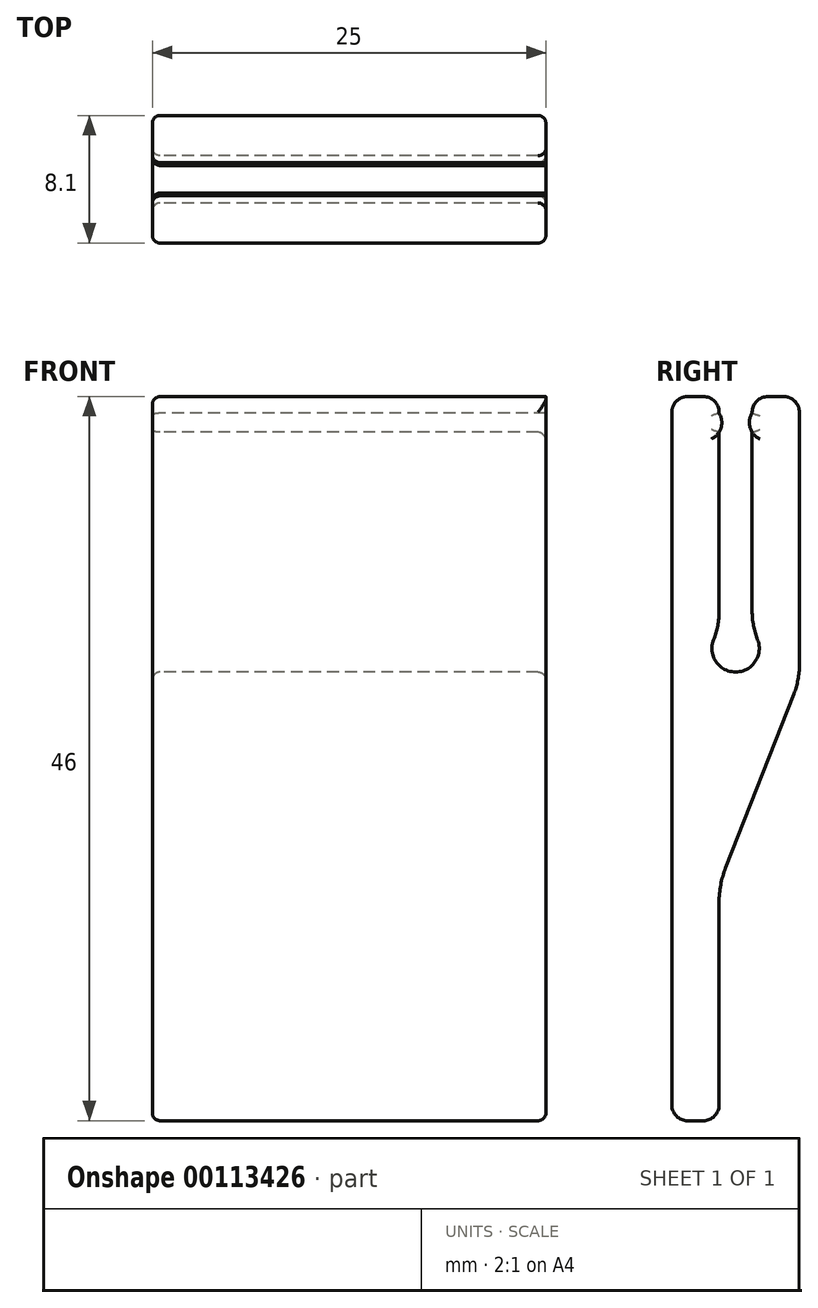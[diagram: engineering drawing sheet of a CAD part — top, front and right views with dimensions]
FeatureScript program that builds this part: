
annotation { "Feature Type Name" : "Feature", "Feature Type Description" : "" }
export const myFeature = defineFeature(function(context is Context, id is Id, definition is map)
    precondition{}
    {
        {
            var Q0;
            Q0=qCreatedBy(makeId("Right.planeOp"),FACE);
            var sketch = newSketch(context, id + "F0", { "sketchPlane" : qUnion([Q0])});
            skLineSegment(sketch, "E0.bottom", {"start": v(-2.62, 41.62) * mm, "end": v(0.38, 41.62) * mm});
            skLineSegment(sketch, "E0.left", {"start": v(-2.62, 41.62) * mm, "end": v(-2.62, 25.62) * mm});
            skLineSegment(sketch, "E0.right", {"start": v(5.48, 41.62) * mm, "end": v(5.48, 23.62) * mm});
            skLineSegment(sketch, "E1.top", {"start": v(-2.62, -4.38) * mm, "end": v(0.38, -4.38) * mm});
            skLineSegment(sketch, "E1.left", {"start": v(-2.62, 25.62) * mm, "end": v(-2.62, -4.38) * mm});
            skLineSegment(sketch, "E1.right", {"start": v(0.38, 9.48) * mm, "end": v(0.38, -4.38) * mm});
            skLineSegment(sketch, "E2.left", {"start": v(0.38, 41.62) * mm, "end": v(0.38, 26.69) * mm});
            skLineSegment(sketch, "E2.right", {"start": v(2.48, 41.62) * mm, "end": v(2.48, 26.69) * mm});
            skLineSegment(sketch, "E3.trimOffspring", {"start": v(2.48, 41.62) * mm, "end": v(5.48, 41.62) * mm});
            skLineSegment(sketch, "E4", {"start": v(5.48, 23.62) * mm, "end": v(0.8, 11.67) * mm});
            skLineSegment(sketch, "E5.filletArc", {"start": v(0.6, 24.36) * mm, "end": v(0.6, 24.36) * mm});
            skPoint(sketch, "E6.visualSharp", {"position": v(0.38, 10.62) * mm});
            skArc(sketch, "E6.filletArc", {"start": v(0.8, 11.67) * mm, "mid": v(0.48, 10.6) * mm, "end": v(0.38, 9.48) * mm});
            skArc(sketch, "E7", {"start": v(0.38, 26.69) * mm, "mid": v(1.43, 24.12) * mm, "end": v(2.48, 26.69) * mm});
            skLineSegment(sketch, "E8", {"start": v(0.38, 25.62) * mm, "end": v(2.48, 25.62) * mm, "construction": true});
            skCircle(sketch, "E9", {"center": v(-0.57, 39.95) * mm, "radius": 1.13 * mm});
            skLineSegment(sketch, "E10", {"start": v(1.43, 25.62) * mm, "end": v(1.43, 44.61) * mm, "construction": true});
            skCircle(sketch, "E11.MirrorC", {"center": v(3.43, 39.95) * mm, "radius": 1.13 * mm});
            skLineSegment(sketch, "E12", {"start": v(0.38, 28.92) * mm, "end": v(2.48, 28.92) * mm, "construction": true});
            skPoint(sketch, "E13", {"position": v(1.43, 28.92) * mm});
            skSolve(sketch);
        }
        {
            var Q0;
            Q0 = qSketchRegion(id + "F0", true);
            extrude(context, id + "F1", {"entities" : qUnion([Q0]), "depth" : 25 * mm});
        }
        {
            var Q0;
            Q0=makeQuery(id+"F1.opExtrude","SWEPT_EDGE",EDGE,{"disambiguationData":[OSD([sQuery(id+"F0.wireOp",EDGE,"E2.left"),sQuery(id+"F0.wireOp",EDGE,"E7")])]});
            var Q1;
            Q1=makeQuery(id+"F1.opExtrude","SWEPT_EDGE",EDGE,{"disambiguationData":[OSD([sQuery(id+"F0.wireOp",EDGE,"E2.right"),sQuery(id+"F0.wireOp",EDGE,"E7")])]});
            var Q2;
            Q2=makeQuery(id+"F1.opExtrude","SWEPT_EDGE",EDGE,{"disambiguationData":[OSD([sQuery(id+"F0.wireOp",EDGE,"E0.right"),sQuery(id+"F0.wireOp",EDGE,"E4")])]});
            fillet(context, id + "F2", {"entities" : qUnion([Q0, Q1, Q2]), "radius" : 5 * mm, "tangentPropagation" : true, "allowEdgeOverflow" : false});
        }
        {
            var Q0;
            Q0=makeQuery(id+"F1.opExtrude","SWEPT_EDGE",EDGE,{"disambiguationData":[OSD([sQuery(id+"F0.wireOp",EDGE,"E0.bottom"),sQuery(id+"F0.wireOp",EDGE,"E0.left")])]});
            var Q1;
            Q1=makeQuery(id+"F1.opExtrude","SWEPT_EDGE",EDGE,{"disambiguationData":[OSD([sQuery(id+"F0.wireOp",EDGE,"E0.bottom"),sQuery(id+"F0.wireOp",EDGE,"E2.left")])]});
            var Q2;
            Q2=makeQuery(id+"F1.opExtrude","SWEPT_EDGE",EDGE,{"disambiguationData":[OSD([sQuery(id+"F0.wireOp",EDGE,"E2.right"),sQuery(id+"F0.wireOp",EDGE,"E3.trimOffspring")])]});
            var Q3;
            Q3=makeQuery(id+"F1.opExtrude","SWEPT_EDGE",EDGE,{"disambiguationData":[OSD([sQuery(id+"F0.wireOp",EDGE,"E0.right"),sQuery(id+"F0.wireOp",EDGE,"E3.trimOffspring")])]});
            var Q4;
            Q4=makeQuery(id+"F1.opExtrude","SWEPT_EDGE",EDGE,{"disambiguationData":[OSD([sQuery(id+"F0.wireOp",EDGE,"E1.top"),sQuery(id+"F0.wireOp",EDGE,"E1.left")])]});
            var Q5;
            Q5=makeQuery(id+"F1.opExtrude","SWEPT_EDGE",EDGE,{"disambiguationData":[OSD([sQuery(id+"F0.wireOp",EDGE,"E1.top"),sQuery(id+"F0.wireOp",EDGE,"E1.right")])]});
            fillet(context, id + "F3", {"entities" : qUnion([Q0, Q1, Q2, Q3, Q4, Q5]), "radius" : 1 * mm, "tangentPropagation" : true, "allowEdgeOverflow" : false});
        }
        {
            var Q0;
            Q0=makeQuery(id+"F1.opExtrude","CAP_EDGE",EDGE,{"disambiguationData":[OSD([sQuery(id+"F0.wireOp",EDGE,"E0.left"),sQuery(id+"F0.wireOp",EDGE,"E1.left")])],"isStart":false});
            var Q1;
            Q1=makeQuery(id+"F1.opExtrude","CAP_EDGE",EDGE,{"disambiguationData":[OSD([sQuery(id+"F0.wireOp",EDGE,"E0.left"),sQuery(id+"F0.wireOp",EDGE,"E1.left")])],"isStart":true});
            var Q2;
            Q2=makeQuery(id+"F1.opExtrude","CAP_EDGE",EDGE,{"disambiguationData":[OSD([sQuery(id+"F0.wireOp",EDGE,"E0.right")])],"isStart":true});
            var Q3;
            Q3=makeQuery(id+"F1.opExtrude","CAP_EDGE",EDGE,{"disambiguationData":[OSD([sQuery(id+"F0.wireOp",EDGE,"E4")])],"isStart":true});
            var Q4;
            Q4=makeQuery(id+"F1.opExtrude","CAP_EDGE",EDGE,{"disambiguationData":[OSD([sQuery(id+"F0.wireOp",EDGE,"E0.right")])],"isStart":false});
            var Q5;
            Q5=makeQuery(id+"F1.opExtrude","CAP_EDGE",EDGE,{"disambiguationData":[OSD([sQuery(id+"F0.wireOp",EDGE,"E4")])],"isStart":false});
            fillet(context, id + "F4", {"entities" : qUnion([Q0, Q1, Q2, Q3, Q4, Q5]), "radius" : 0.5 * mm, "allowEdgeOverflow" : false});
        }
        {
            var Q0;
            {var subQ0=sQuery(id+"F0.wireOp",EDGE,"E2.right");Q0=makeQuery(id+"F1.opExtrude","CAP_EDGE",EDGE,{"disambiguationData":[OSD([subQ0]),TDD([makeQuery(id+"F0.imprint","IMPRINT",EDGE,{"disambiguationData":[TD([[makeQuery(id+"F0.imprint","INTERSECT",VERTEX,{"derivedFrom":[subQ0,sQuery(id+"F0.wireOp",EDGE,"E7")]}),1.0]])],"derivedFrom":subQ0})])],"isStart":true});}
            var Q1;
            Q1=makeQuery(id+"F1.opExtrude","CAP_EDGE",EDGE,{"disambiguationData":[OSD([sQuery(id+"F0.wireOp",EDGE,"E11.MirrorC")])],"isStart":true});
            var Q2;
            Q2=makeQuery(id+"F1.opExtrude","CAP_EDGE",EDGE,{"disambiguationData":[OSD([sQuery(id+"F0.wireOp",EDGE,"E9")])],"isStart":true});
            var Q3;
            {var subQ0=sQuery(id+"F0.wireOp",EDGE,"E3.trimOffspring");var subQ1=sQuery(id+"F0.wireOp",EDGE,"E2.right");Q3=makeQuery(id+"F3.opFillet","BLEND_EDGE",EDGE,{"blendedFrom":[makeQuery(id+"F1.opExtrude","SWEPT_EDGE",EDGE,{"disambiguationData":[OSD([subQ1,subQ0])]}),makeQuery(id+"F1.opExtrude","CAP_FACE",FACE,{"disambiguationData":[OSD([sQuery(id+"F0.wireOp",EDGE,"E0.bottom"),sQuery(id+"F0.wireOp",EDGE,"E0.left"),sQuery(id+"F0.wireOp",EDGE,"E0.right"),sQuery(id+"F0.wireOp",EDGE,"E1.top"),sQuery(id+"F0.wireOp",EDGE,"E1.left"),sQuery(id+"F0.wireOp",EDGE,"E1.right"),sQuery(id+"F0.wireOp",EDGE,"E2.left"),subQ1,subQ0,sQuery(id+"F0.wireOp",EDGE,"E4"),sQuery(id+"F0.wireOp",EDGE,"E6.filletArc"),sQuery(id+"F0.wireOp",EDGE,"E7"),sQuery(id+"F0.wireOp",EDGE,"E9"),sQuery(id+"F0.wireOp",EDGE,"E11.MirrorC")])],"isStart":true})],"blendedInto":[makeQuery(id+"F1.opExtrude","CAP_FACE",FACE,{"disambiguationData":[OSD([sQuery(id+"F0.wireOp",EDGE,"E0.bottom"),sQuery(id+"F0.wireOp",EDGE,"E0.left"),sQuery(id+"F0.wireOp",EDGE,"E0.right"),sQuery(id+"F0.wireOp",EDGE,"E1.top"),sQuery(id+"F0.wireOp",EDGE,"E1.left"),sQuery(id+"F0.wireOp",EDGE,"E1.right"),sQuery(id+"F0.wireOp",EDGE,"E2.left"),subQ1,subQ0,sQuery(id+"F0.wireOp",EDGE,"E4"),sQuery(id+"F0.wireOp",EDGE,"E6.filletArc"),sQuery(id+"F0.wireOp",EDGE,"E7"),sQuery(id+"F0.wireOp",EDGE,"E9"),sQuery(id+"F0.wireOp",EDGE,"E11.MirrorC")])],"isStart":true})]});}
            var Q4;
            {var subQ0=sQuery(id+"F0.wireOp",EDGE,"E2.left");var subQ1=sQuery(id+"F0.wireOp",EDGE,"E0.bottom");Q4=makeQuery(id+"F3.opFillet","BLEND_EDGE",EDGE,{"blendedFrom":[makeQuery(id+"F1.opExtrude","SWEPT_EDGE",EDGE,{"disambiguationData":[OSD([subQ1,subQ0])]}),makeQuery(id+"F1.opExtrude","CAP_FACE",FACE,{"disambiguationData":[OSD([subQ1,sQuery(id+"F0.wireOp",EDGE,"E0.left"),sQuery(id+"F0.wireOp",EDGE,"E0.right"),sQuery(id+"F0.wireOp",EDGE,"E1.top"),sQuery(id+"F0.wireOp",EDGE,"E1.left"),sQuery(id+"F0.wireOp",EDGE,"E1.right"),subQ0,sQuery(id+"F0.wireOp",EDGE,"E2.right"),sQuery(id+"F0.wireOp",EDGE,"E3.trimOffspring"),sQuery(id+"F0.wireOp",EDGE,"E4"),sQuery(id+"F0.wireOp",EDGE,"E6.filletArc"),sQuery(id+"F0.wireOp",EDGE,"E7"),sQuery(id+"F0.wireOp",EDGE,"E9"),sQuery(id+"F0.wireOp",EDGE,"E11.MirrorC")])],"isStart":true})],"blendedInto":[makeQuery(id+"F1.opExtrude","CAP_FACE",FACE,{"disambiguationData":[OSD([subQ1,sQuery(id+"F0.wireOp",EDGE,"E0.left"),sQuery(id+"F0.wireOp",EDGE,"E0.right"),sQuery(id+"F0.wireOp",EDGE,"E1.top"),sQuery(id+"F0.wireOp",EDGE,"E1.left"),sQuery(id+"F0.wireOp",EDGE,"E1.right"),subQ0,sQuery(id+"F0.wireOp",EDGE,"E2.right"),sQuery(id+"F0.wireOp",EDGE,"E3.trimOffspring"),sQuery(id+"F0.wireOp",EDGE,"E4"),sQuery(id+"F0.wireOp",EDGE,"E6.filletArc"),sQuery(id+"F0.wireOp",EDGE,"E7"),sQuery(id+"F0.wireOp",EDGE,"E9"),sQuery(id+"F0.wireOp",EDGE,"E11.MirrorC")])],"isStart":true})]});}
            var Q5;
            {var subQ0=sQuery(id+"F0.wireOp",EDGE,"E2.left");Q5=makeQuery(id+"F1.opExtrude","CAP_EDGE",EDGE,{"disambiguationData":[OSD([subQ0]),TDD([makeQuery(id+"F0.imprint","IMPRINT",EDGE,{"disambiguationData":[TD([[makeQuery(id+"F0.imprint","INTERSECT",VERTEX,{"derivedFrom":[subQ0,sQuery(id+"F0.wireOp",EDGE,"E7")]}),1.0]])],"derivedFrom":subQ0})])],"isStart":false});}
            fillet(context, id + "F5", {"entities" : qUnion([Q0, Q1, Q2, Q3, Q4, Q5]), "radius" : 0.5 * mm, "tangentPropagation" : true, "allowEdgeOverflow" : false});
        }
    });
